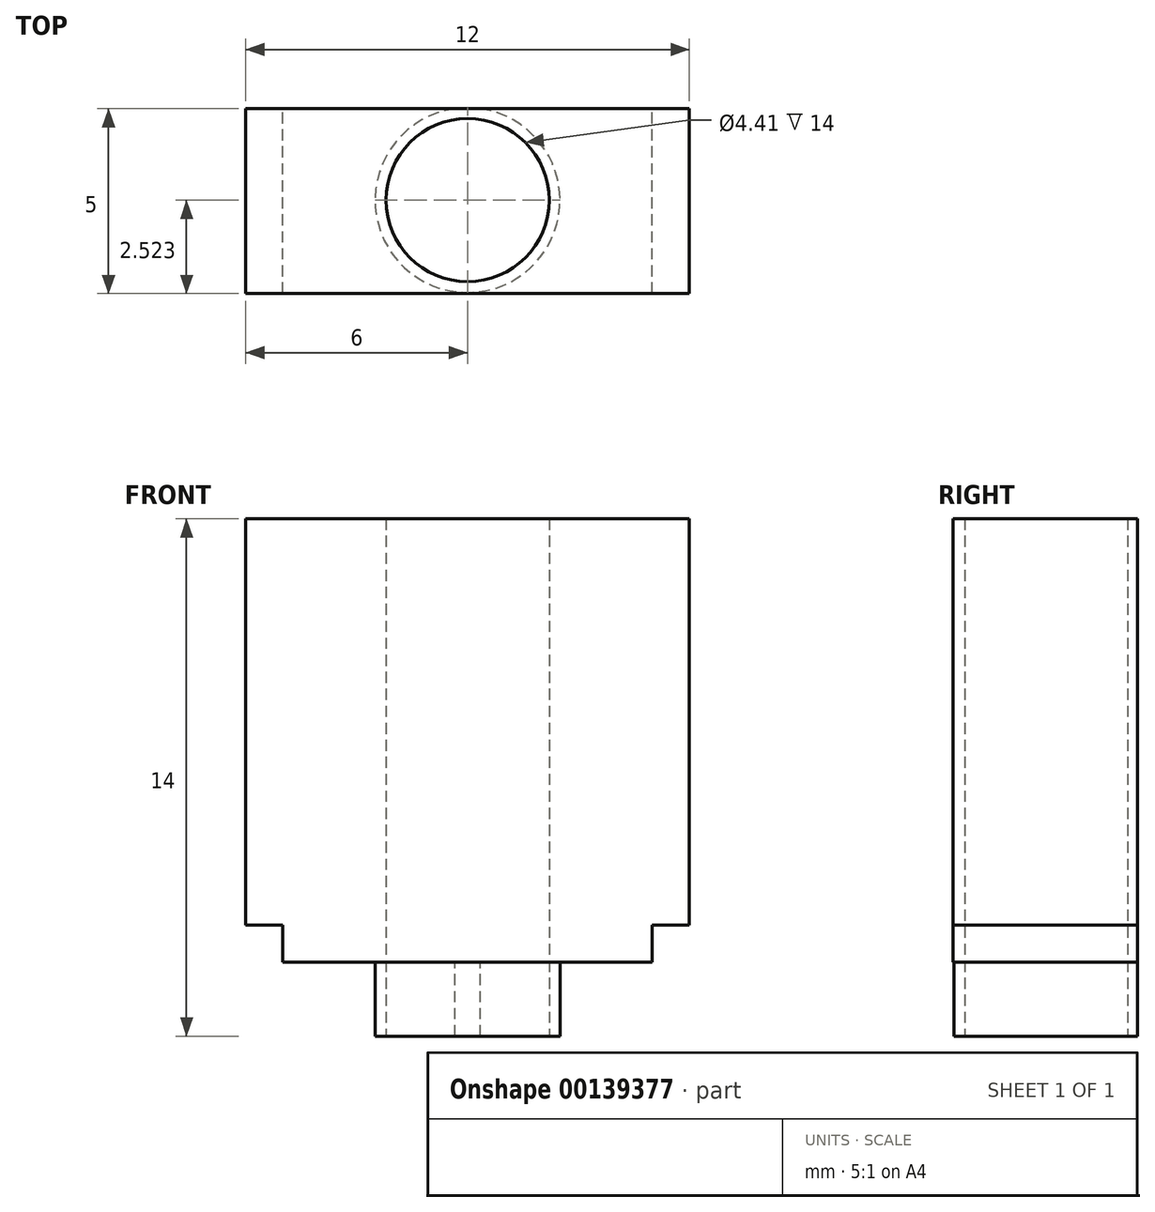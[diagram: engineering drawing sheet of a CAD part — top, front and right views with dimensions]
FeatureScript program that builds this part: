
annotation { "Feature Type Name" : "Feature", "Feature Type Description" : "" }
export const myFeature = defineFeature(function(context is Context, id is Id, definition is map)
    precondition{}
    {
        {
            var Q0;
            Q0=qCreatedBy(makeId("Front.planeOp"),FACE);
            var sketch = newSketch(context, id + "F0", { "sketchPlane" : qUnion([Q0])});
            skLineSegment(sketch, "E0.bottom", {"start": v(-12, 11) * mm, "end": v(0, 11) * mm});
            skLineSegment(sketch, "E0.top", {"start": v(-12, 0) * mm, "end": v(-11, 0) * mm});
            skLineSegment(sketch, "E0.left", {"start": v(-12, 11) * mm, "end": v(-12, 0) * mm});
            skLineSegment(sketch, "E0.right", {"start": v(0, 11) * mm, "end": v(0, 0) * mm});
            skLineSegment(sketch, "E1", {"start": v(-11, 0) * mm, "end": v(-11, -1) * mm});
            skLineSegment(sketch, "E2", {"start": v(-11, -1) * mm, "end": v(-1, -1) * mm});
            skLineSegment(sketch, "E3", {"start": v(-1, -1) * mm, "end": v(-1, 0) * mm});
            skLineSegment(sketch, "E4.trimOffspring", {"start": v(-1, 0) * mm, "end": v(0, 0) * mm});
            skSolve(sketch);
        }
        {
            var Q0;
            Q0=makeQuery(id+"F0.imprint","IMPRINT",FACE,{"disambiguationData":[TD([[makeQuery(id+"F0.imprint","IMPRINT",EDGE,{"derivedFrom":sQuery(id+"F0.wireOp",EDGE,"E0.bottom")}),-1.0]])]});
            extrude(context, id + "F1", {"entities" : qUnion([Q0]), "depth" : 5 * mm});
        }
        {
            var Q0;
            Q0=makeQuery(id+"F1.opExtrude","SWEPT_FACE",FACE,{"disambiguationData":[OSD([sQuery(id+"F0.wireOp",EDGE,"E2")])]});
            var sketch = newSketch(context, id + "F2", { "sketchPlane" : qUnion([Q0])});
            skCircle(sketch, "E5", {"center": v(-6, 2.48) * mm, "radius": 2.5 * mm});
            skSolve(sketch);
        }
        {
            var Q0;
            {var subQ0=sQuery(id+"F2.wireOp",EDGE,"E5");var subQ1=makeQuery(id+"F1.opExtrude","CAP_EDGE",EDGE,{"disambiguationData":[OSD([sQuery(id+"F0.wireOp",EDGE,"E2")])],"isStart":true});var subQ2=makeQuery(id+"F2.imprint","INTERSECT",VERTEX,{"disambiguationData":[OD(0.0)],"derivedFrom":[subQ1,subQ0]});Q0=makeQuery(id+"F2.imprint","IMPRINT",FACE,{"disambiguationData":[TD([[makeQuery(id+"F2.imprint","IMPRINT",EDGE,{"disambiguationData":[TD([[subQ2,1.0]])],"derivedFrom":subQ0}),1.0]])]});}
            extrude(context, id + "F3", {"entities" : qUnion([Q0]), "operationType" : NewBodyOperationType.ADD, "depth" : 2 * mm});
        }
        {
            var Q0;
            Q0=makeQuery(id+"F3.opExtrude","CAP_FACE",FACE,{"disambiguationData":[OSD([sQuery(id+"F0.wireOp",EDGE,"E2"),sQuery(id+"F2.wireOp",EDGE,"E5")])],"isStart":false});
            var sketch = newSketch(context, id + "F4", { "sketchPlane" : qUnion([Q0])});
            skCircle(sketch, "E6", {"center": v(-6, 2.48) * mm, "radius": 2.2 * mm});
            skSolve(sketch);
        }
        {
            var Q0;
            Q0=makeQuery(id+"F4.imprint","IMPRINT",FACE,{"disambiguationData":[TD([[makeQuery(id+"F4.imprint","IMPRINT",EDGE,{"derivedFrom":sQuery(id+"F4.wireOp",EDGE,"E6")}),1.0]])]});
            extrude(context, id + "F5", {"entities" : qUnion([Q0]), "operationType" : NewBodyOperationType.REMOVE, "oppositeDirection" : true, "depth" : 25 * mm});
        }
    });
